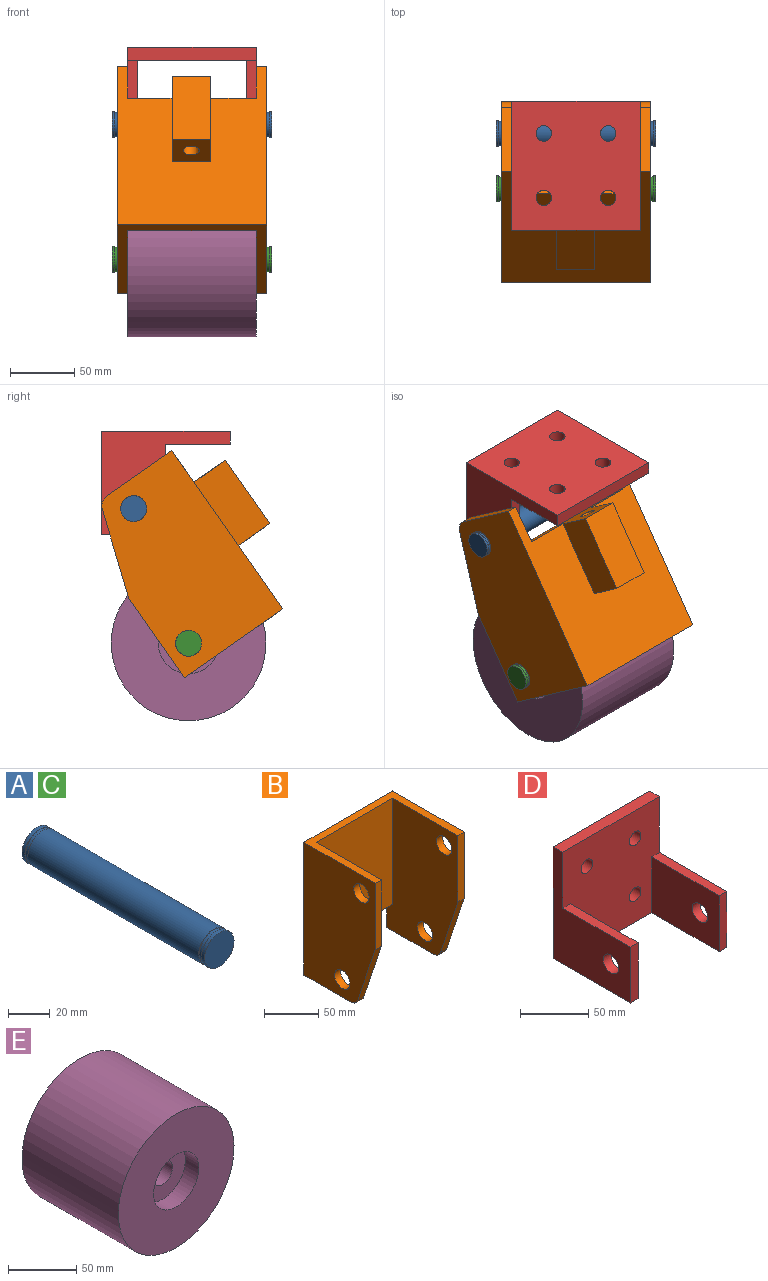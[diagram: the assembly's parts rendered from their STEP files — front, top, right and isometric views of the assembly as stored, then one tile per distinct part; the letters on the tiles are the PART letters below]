
ASSEMBLY  parts=5 mates=4
PART A: 11 faces, bbox 20x124x20 mm
  f0: cylinder r=10mm len=116mm, axis (0,1,0), area 7288.5mm2, adj f2,f7
  f1: cylinder r=9.5mm len=19mm, axis (0,-1,0), area 119.4mm2, adj f2,f3
  f2: plane 20x20mm, normal (0,-1,0), area 30.6mm2, adj f0,f1
  f3: plane 20x20mm, normal (0,1,0), area 30.6mm2, adj f1,f5
  f4: plane 20x20mm, normal (0,-1,0), area 314.2mm2, adj f5
  f5: cylinder r=10mm len=20mm, axis (0,1,0), area 125.7mm2, adj f3,f4
  f6: cylinder r=9.5mm len=19mm, axis (0,1,0), area 119.4mm2, adj f7,f8
  f7: plane 20x20mm, normal (0,1,0), area 30.6mm2, adj f0,f6
  f8: plane 20x20mm, normal (0,-1,0), area 30.6mm2, adj f6,f10
  f9: plane 20x20mm, normal (0,1,0), area 314.2mm2, adj f10
  f10: cylinder r=10mm len=20mm, axis (0,1,0), area 125.7mm2, adj f8,f9
PART B: 25 faces, bbox 116x123x150 mm
  f0: plane 120x100mm, normal (0,-1,0), area 12000mm2, adj f3,f7,f9,f17
  f1: plane 60.79x8mm, normal (0,0,-1), area 486.3mm2, adj f5,f6,f9,f24
  f2: plane 150x93mm, normal (-1,0,0), area 12374.6mm2, adj f3,f4,f6,f8,f14,f15,f16,f23
  f3: plane 116x93mm, normal (0,0,1), area 2288mm2, adj f0,f2,f5,f6,f7,f8,f9,f10
  f4: plane 60.79x8mm, normal (0,0,-1), area 486.3mm2, adj f2,f6,f7,f23
  f5: plane 150x93mm, normal (1,0,0), area 12374.6mm2, adj f1,f3,f6,f10,f11,f12,f13,f24
  f6: plane 150x116mm, normal (0,1,0), area 12600mm2, adj f1,f2,f3,f4,f5,f7,f9,f17
  f7: plane 150x93mm, normal (1,0,0), area 11414.6mm2, adj f0,f3,f4,f6,f8,f14,f15,f16
  f8: plane 75x8mm, normal (0,-1,0), area 600mm2, adj f2,f3,f7,f14
  f9: plane 150x93mm, normal (-1,0,0), area 11414.6mm2, adj f0,f1,f3,f6,f10,f11,f12,f13
  f10: plane 75x8mm, normal (0,-1,0), area 600mm2, adj f3,f5,f9,f11
  f11: plane 68.16x22.72mm, normal (0,-0.95,-0.32), area 574.8mm2, adj f5,f9,f10,f24
  f12: cylinder r=10mm len=20mm, axis (-1,0,0), area 502.7mm2, adj f5,f9
  f13: cylinder r=10mm len=20mm, axis (-1,0,0), area 502.7mm2, adj f5,f9
  f14: plane 68.16x22.72mm, normal (0,-0.95,-0.32), area 574.8mm2, adj f2,f7,f8,f23
  f15: cylinder r=10mm len=20mm, axis (-1,0,0), area 502.7mm2, adj f2,f7
  f16: cylinder r=10mm len=20mm, axis (-1,0,0), area 502.7mm2, adj f2,f7
  f17: plane 100x38mm, normal (0,0,-1), area 1586.9mm2, adj f0,f6,f7,f9,f18,f19,f21,f22
  f18: plane 60x30mm, normal (1,0,0), area 1800mm2, adj f6,f17,f20,f21
  f19: plane 60x30mm, normal (-1,0,0), area 1800mm2, adj f6,f17,f20,f21
  f20: plane 30x30mm, normal (0,0,1), area 786.9mm2, adj f6,f18,f19,f21,f22
  f21: plane 60x30mm, normal (0,1,0), area 1800mm2, adj f17,f18,f19,f20
  f22: cylinder r=6mm len=60mm, axis (0,0,1), area 2261.9mm2, adj f17,f20
  f23: cylinder r=10mm len=9.49mm, axis (-1,0,0), area 99.9mm2, adj f2,f4,f7,f14
  f24: cylinder r=10mm len=9.49mm, axis (-1,0,0), area 99.9mm2, adj f1,f5,f9,f11
PART C: same geometry as A
PART D: 18 faces, bbox 100x80x100 mm
  f0: plane 100x100mm, normal (0,-1,0), area 8747.6mm2, adj f1,f2,f3,f4,f5,f6,f7,f8
  f1: plane 100x10mm, normal (0,0,1), area 1000mm2, adj f0,f2,f8,f9
  f2: plane 100x80mm, normal (-1,0,0), area 4298.9mm2, adj f0,f1,f3,f9,f10,f12,f17
  f3: plane 100x80mm, normal (0,0,-1), area 2120mm2, adj f0,f2,f8,f9,f11,f12,f14,f15
  f4: cylinder r=6mm len=12mm, axis (0,1,0), area 377mm2, adj f0,f9
  f5: cylinder r=6mm len=12mm, axis (0,1,0), area 377mm2, adj f0,f9
  f6: cylinder r=6mm len=12mm, axis (0,1,0), area 377mm2, adj f0,f9
  f7: cylinder r=6mm len=12mm, axis (0,1,0), area 377mm2, adj f0,f9
  f8: plane 100x80mm, normal (1,0,0), area 4298.9mm2, adj f0,f1,f3,f9,f13,f15,f16
  f9: plane 100x100mm, normal (0,1,0), area 9547.6mm2, adj f1,f2,f3,f4,f5,f6,f7,f8
  f10: plane 70x8mm, normal (0,0,1), area 560mm2, adj f0,f2,f11,f12
  f11: plane 70x50mm, normal (1,0,0), area 3298.9mm2, adj f0,f3,f10,f12,f17
  f12: plane 50x8mm, normal (0,-1,0), area 400mm2, adj f2,f3,f10,f11
  f13: plane 70x8mm, normal (0,0,1), area 560mm2, adj f0,f8,f14,f15
  f14: plane 70x50mm, normal (-1,0,0), area 3298.9mm2, adj f0,f3,f13,f15,f16
  f15: plane 50x8mm, normal (0,-1,0), area 400mm2, adj f3,f8,f13,f14
  f16: cylinder r=8mm len=16mm, axis (-1,0,0), area 402.1mm2, adj f8,f14
  f17: cylinder r=8mm len=16mm, axis (-1,0,0), area 402.1mm2, adj f2,f11
PART E: 8 faces, bbox 120x100x120 mm
  f0: cylinder r=10.25mm len=72mm, axis (0,1,0), area 4637mm2, adj f5,f7
  f1: cylinder r=60mm len=120mm, axis (0,1,0), area 37699.1mm2, adj f2,f3
  f2: plane 120x120mm, normal (0,-1,0), area 9574.8mm2, adj f1,f4
  f3: plane 120x120mm, normal (0,1,0), area 9574.8mm2, adj f1,f6
  f4: cylinder r=23.5mm len=47mm, axis (0,-1,0), area 2067.2mm2, adj f2,f5
  f5: plane 47x47mm, normal (0,-1,0), area 1404.9mm2, adj f0,f4
  f6: cylinder r=23.5mm len=47mm, axis (0,1,0), area 2067.2mm2, adj f3,f7
  f7: plane 47x47mm, normal (0,1,0), area 1404.9mm2, adj f0,f6
PLACE A rot(axis=(0.69,0.69,-0.22),155.4deg) t=(78.42,-97.06,-149.34)mm
PLACE B rot(axis=(1,0,0),145deg) t=(35.34,-155.59,-145.75)mm
PLACE C rot(axis=(0.58,-0.58,0.58),120deg) t=(-45.58,-139.68,-253.79)mm
PLACE D rot(axis=(1,0,0),90deg) t=(16.42,-122.06,-89.34)mm
PLACE E rot(axis=(0,0,1),90deg) t=(-33.58,-139.68,-253.79)mm
MATE revolute A.f0 <-> B.f12  axis (1,0,0) through (16.42,-97.06,-149.34)mm
MATE revolute C.f0 <-> E.f0  axis (-1,0,0) through (16.42,-139.68,-253.79)mm
MATE revolute A.f0 <-> D.f16  axis (1,0,0) through (16.42,-97.06,-149.34)mm
MATE revolute C.f0 <-> B.f13  axis (-1,0,0) through (16.42,-139.68,-253.79)mm
